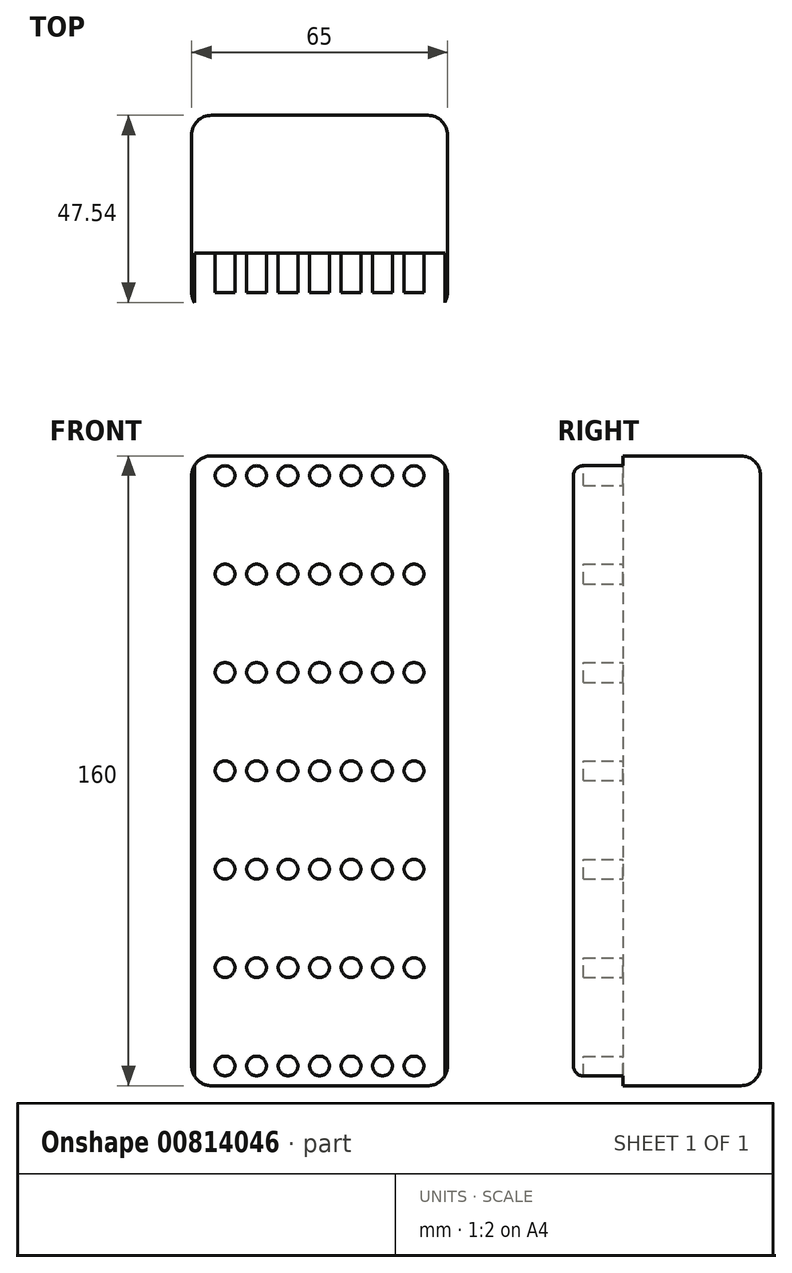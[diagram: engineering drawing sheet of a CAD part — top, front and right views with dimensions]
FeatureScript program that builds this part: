
annotation { "Feature Type Name" : "Feature", "Feature Type Description" : "" }
export const myFeature = defineFeature(function(context is Context, id is Id, definition is map)
    precondition{}
    {
        {
            var Q0;
            Q0=qCreatedBy(makeId("Front.planeOp"),FACE);
            var sketch = newSketch(context, id + "F0", { "sketchPlane" : qUnion([Q0])});
            skLineSegment(sketch, "E0.bottom", {"start": v(-32.5, 80) * mm, "end": v(32.5, 80) * mm});
            skLineSegment(sketch, "E0.top", {"start": v(-32.5, -80) * mm, "end": v(32.5, -80) * mm});
            skLineSegment(sketch, "E0.left", {"start": v(-32.5, 80) * mm, "end": v(-32.5, -80) * mm});
            skLineSegment(sketch, "E0.right", {"start": v(32.5, 80) * mm, "end": v(32.5, -80) * mm});
            skPoint(sketch, "E0.middle", {"position": v(0, 0) * mm});
            skSolve(sketch);
        }
        {
            var Q0;
            Q0 = qSketchRegion(id + "F0", true);
            extrude(context, id + "F1", {"entities" : qUnion([Q0]), "depth" : 50 * mm, "offsetDistance" : 25 * mm});
        }
        {
            var Q0;
            Q0=makeQuery(id+"F1.opExtrude","SWEPT_EDGE",EDGE,{"disambiguationData":[OSD([sQuery(id+"F0.wireOp",EDGE,"E0.bottom"),sQuery(id+"F0.wireOp",EDGE,"E0.right")])]});
            var Q1;
            Q1=makeQuery(id+"F1.opExtrude","SWEPT_EDGE",EDGE,{"disambiguationData":[OSD([sQuery(id+"F0.wireOp",EDGE,"E0.bottom"),sQuery(id+"F0.wireOp",EDGE,"E0.left")])]});
            var Q2;
            Q2=makeQuery(id+"F1.opExtrude","CAP_EDGE",EDGE,{"disambiguationData":[OSD([sQuery(id+"F0.wireOp",EDGE,"E0.bottom")])],"isStart":true});
            var Q3;
            Q3=makeQuery(id+"F1.opExtrude","CAP_EDGE",EDGE,{"disambiguationData":[OSD([sQuery(id+"F0.wireOp",EDGE,"E0.right")])],"isStart":true});
            var Q4;
            Q4=makeQuery(id+"F1.opExtrude","CAP_EDGE",EDGE,{"disambiguationData":[OSD([sQuery(id+"F0.wireOp",EDGE,"E0.right")])],"isStart":false});
            var Q5;
            Q5=makeQuery(id+"F1.opExtrude","CAP_EDGE",EDGE,{"disambiguationData":[OSD([sQuery(id+"F0.wireOp",EDGE,"E0.left")])],"isStart":false});
            var Q6;
            Q6=makeQuery(id+"F1.opExtrude","CAP_EDGE",EDGE,{"disambiguationData":[OSD([sQuery(id+"F0.wireOp",EDGE,"E0.top")])],"isStart":false});
            var Q7;
            Q7=makeQuery(id+"F1.opExtrude","SWEPT_EDGE",EDGE,{"disambiguationData":[OSD([sQuery(id+"F0.wireOp",EDGE,"E0.top"),sQuery(id+"F0.wireOp",EDGE,"E0.right")])]});
            var Q8;
            Q8=makeQuery(id+"F1.opExtrude","SWEPT_EDGE",EDGE,{"disambiguationData":[OSD([sQuery(id+"F0.wireOp",EDGE,"E0.top"),sQuery(id+"F0.wireOp",EDGE,"E0.left")])]});
            var Q9;
            Q9=makeQuery(id+"F1.opExtrude","CAP_EDGE",EDGE,{"disambiguationData":[OSD([sQuery(id+"F0.wireOp",EDGE,"E0.top")])],"isStart":true});
            var Q10;
            Q10=makeQuery(id+"F1.opExtrude","CAP_EDGE",EDGE,{"disambiguationData":[OSD([sQuery(id+"F0.wireOp",EDGE,"E0.left")])],"isStart":true});
            var Q11;
            Q11=makeQuery(id+"F1.opExtrude","CAP_EDGE",EDGE,{"disambiguationData":[OSD([sQuery(id+"F0.wireOp",EDGE,"E0.bottom")])],"isStart":false});
            fillet(context, id + "F2", {"entities" : qUnion([Q0, Q1, Q2, Q3, Q4, Q5, Q6, Q7, Q8, Q9, Q10, Q11]), "radius" : 5 * mm, "tangentPropagation" : true, "allowEdgeOverflow" : false});
        }
        {
            var Q0;
            Q0=makeQuery(id+"F1.opExtrude","CAP_FACE",FACE,{"disambiguationData":[OSD([sQuery(id+"F0.wireOp",EDGE,"E0.bottom"),sQuery(id+"F0.wireOp",EDGE,"E0.top"),sQuery(id+"F0.wireOp",EDGE,"E0.left"),sQuery(id+"F0.wireOp",EDGE,"E0.right")])],"isStart":false});
            var sketch = newSketch(context, id + "F3", { "sketchPlane" : qUnion([Q0])});
            skLineSegment(sketch, "E1.bottom", {"start": v(-31.8, 81.75) * mm, "end": v(31.8, 81.75) * mm});
            skLineSegment(sketch, "E1.top", {"start": v(-31.8, -81.75) * mm, "end": v(31.8, -81.75) * mm});
            skLineSegment(sketch, "E1.left", {"start": v(-31.8, 81.75) * mm, "end": v(-31.8, -81.75) * mm});
            skLineSegment(sketch, "E1.right", {"start": v(31.8, 81.75) * mm, "end": v(31.8, -81.75) * mm});
            skPoint(sketch, "E1.middle", {"position": v(0, 0) * mm});
            skSolve(sketch);
        }
        {
            var Q0;
            Q0 = qSketchRegion(id + "F3", true);
            extrude(context, id + "F4", {"entities" : qUnion([Q0]), "operationType" : NewBodyOperationType.REMOVE, "oppositeDirection" : true, "depth" : 15 * mm, "offsetDistance" : 25 * mm});
        }
        {
            var Q0;
            Q0=makeQuery(id+"F4.boolean.opBoolean","COPY",FACE,{"derivedFrom":makeQuery(id+"F4.opExtrude","CAP_FACE",FACE,{"disambiguationData":[OSD([sQuery(id+"F3.wireOp",EDGE,"E1.bottom"),sQuery(id+"F3.wireOp",EDGE,"E1.top"),sQuery(id+"F3.wireOp",EDGE,"E1.left"),sQuery(id+"F3.wireOp",EDGE,"E1.right")])],"isStart":false})});
            var sketch = newSketch(context, id + "F5", { "sketchPlane" : qUnion([Q0])});
            skCircle(sketch, "E2", {"center": v(0, 0) * mm, "radius": 2.5 * mm});
            skCircle(sketch, "E3.0.1.0", {"center": v(0, 25) * mm, "radius": 2.5 * mm});
            skCircle(sketch, "E3.0.2.0", {"center": v(0, 50) * mm, "radius": 2.5 * mm});
            skCircle(sketch, "E3.0.3.0", {"center": v(0, 75) * mm, "radius": 2.5 * mm});
            skCircle(sketch, "E3.1.0.0", {"center": v(8, 0) * mm, "radius": 2.5 * mm});
            skCircle(sketch, "E3.1.1.0", {"center": v(8, 25) * mm, "radius": 2.5 * mm});
            skCircle(sketch, "E3.1.2.0", {"center": v(8, 50) * mm, "radius": 2.5 * mm});
            skCircle(sketch, "E3.1.3.0", {"center": v(8, 75) * mm, "radius": 2.5 * mm});
            skCircle(sketch, "E3.2.0.0", {"center": v(16, 0) * mm, "radius": 2.5 * mm});
            skCircle(sketch, "E3.2.1.0", {"center": v(16, 25) * mm, "radius": 2.5 * mm});
            skCircle(sketch, "E3.2.2.0", {"center": v(16, 50) * mm, "radius": 2.5 * mm});
            skCircle(sketch, "E3.2.3.0", {"center": v(16, 75) * mm, "radius": 2.5 * mm});
            skCircle(sketch, "E3.3.0.0", {"center": v(24, 0) * mm, "radius": 2.5 * mm});
            skCircle(sketch, "E3.3.1.0", {"center": v(24, 25) * mm, "radius": 2.5 * mm});
            skCircle(sketch, "E3.3.2.0", {"center": v(24, 50) * mm, "radius": 2.5 * mm});
            skCircle(sketch, "E3.3.3.0", {"center": v(24, 75) * mm, "radius": 2.5 * mm});
            skLineSegment(sketch, "E3.direction1", {"start": v(0, 0) * mm, "end": v(8, 0) * mm, "construction": true});
            skLineSegment(sketch, "E3.direction2", {"start": v(0, 0) * mm, "end": v(0, 25) * mm, "construction": true});
            skCircle(sketch, "E4.MirrorC", {"center": v(-8, 0) * mm, "radius": 2.5 * mm});
            skCircle(sketch, "E5.MirrorC", {"center": v(-24, 0) * mm, "radius": 2.5 * mm});
            skCircle(sketch, "E6.MirrorC", {"center": v(-24, 25) * mm, "radius": 2.5 * mm});
            skCircle(sketch, "E7.MirrorC", {"center": v(-16, 0) * mm, "radius": 2.5 * mm});
            skCircle(sketch, "E8.MirrorC", {"center": v(-24, 50) * mm, "radius": 2.5 * mm});
            skCircle(sketch, "E9.MirrorC", {"center": v(-16, 50) * mm, "radius": 2.5 * mm});
            skCircle(sketch, "E10.MirrorC", {"center": v(-24, 75) * mm, "radius": 2.5 * mm});
            skCircle(sketch, "E11.MirrorC", {"center": v(-8, 75) * mm, "radius": 2.5 * mm});
            skCircle(sketch, "E12.MirrorC", {"center": v(-16, 25) * mm, "radius": 2.5 * mm});
            skCircle(sketch, "E13.MirrorC", {"center": v(-8, 50) * mm, "radius": 2.5 * mm});
            skCircle(sketch, "E14.MirrorC", {"center": v(-16, 75) * mm, "radius": 2.5 * mm});
            skCircle(sketch, "E15.MirrorC", {"center": v(-8, 25) * mm, "radius": 2.5 * mm});
            skLineSegment(sketch, "E16.MirrorCS", {"start": v(0, 0) * mm, "end": v(-8, 0) * mm, "construction": true});
            skCircle(sketch, "E17.MirrorC", {"center": v(0, -25) * mm, "radius": 2.5 * mm});
            skCircle(sketch, "E18.MirrorC", {"center": v(0, -50) * mm, "radius": 2.5 * mm});
            skCircle(sketch, "E19.MirrorC", {"center": v(0, -75) * mm, "radius": 2.5 * mm});
            skCircle(sketch, "E20.MirrorC", {"center": v(16, -25) * mm, "radius": 2.5 * mm});
            skCircle(sketch, "E21.MirrorC", {"center": v(16, -50) * mm, "radius": 2.5 * mm});
            skCircle(sketch, "E22.MirrorC", {"center": v(-16, -25) * mm, "radius": 2.5 * mm});
            skCircle(sketch, "E23.MirrorC", {"center": v(-8, -50) * mm, "radius": 2.5 * mm});
            skCircle(sketch, "E24.MirrorC", {"center": v(24, -25) * mm, "radius": 2.5 * mm});
            skCircle(sketch, "E25.MirrorC", {"center": v(-16, -75) * mm, "radius": 2.5 * mm});
            skCircle(sketch, "E26.MirrorC", {"center": v(-24, -75) * mm, "radius": 2.5 * mm});
            skCircle(sketch, "E27.MirrorC", {"center": v(8, -75) * mm, "radius": 2.5 * mm});
            skCircle(sketch, "E28.MirrorC", {"center": v(24, -50) * mm, "radius": 2.5 * mm});
            skCircle(sketch, "E29.MirrorC", {"center": v(-8, -25) * mm, "radius": 2.5 * mm});
            skCircle(sketch, "E30.MirrorC", {"center": v(-24, -50) * mm, "radius": 2.5 * mm});
            skCircle(sketch, "E31.MirrorC", {"center": v(8, -50) * mm, "radius": 2.5 * mm});
            skCircle(sketch, "E32.MirrorC", {"center": v(24, -75) * mm, "radius": 2.5 * mm});
            skCircle(sketch, "E33.MirrorC", {"center": v(-16, -50) * mm, "radius": 2.5 * mm});
            skCircle(sketch, "E34.MirrorC", {"center": v(8, -25) * mm, "radius": 2.5 * mm});
            skCircle(sketch, "E35.MirrorC", {"center": v(-24, -25) * mm, "radius": 2.5 * mm});
            skCircle(sketch, "E36.MirrorC", {"center": v(-8, -75) * mm, "radius": 2.5 * mm});
            skCircle(sketch, "E37.MirrorC", {"center": v(16, -75) * mm, "radius": 2.5 * mm});
            skSolve(sketch);
        }
        {
            var Q0;
            Q0 = qSketchRegion(id + "F5", true);
            extrude(context, id + "F6", {"entities" : qUnion([Q0]), "operationType" : NewBodyOperationType.ADD, "depth" : 10 * mm, "offsetDistance" : 25 * mm});
        }
    });
